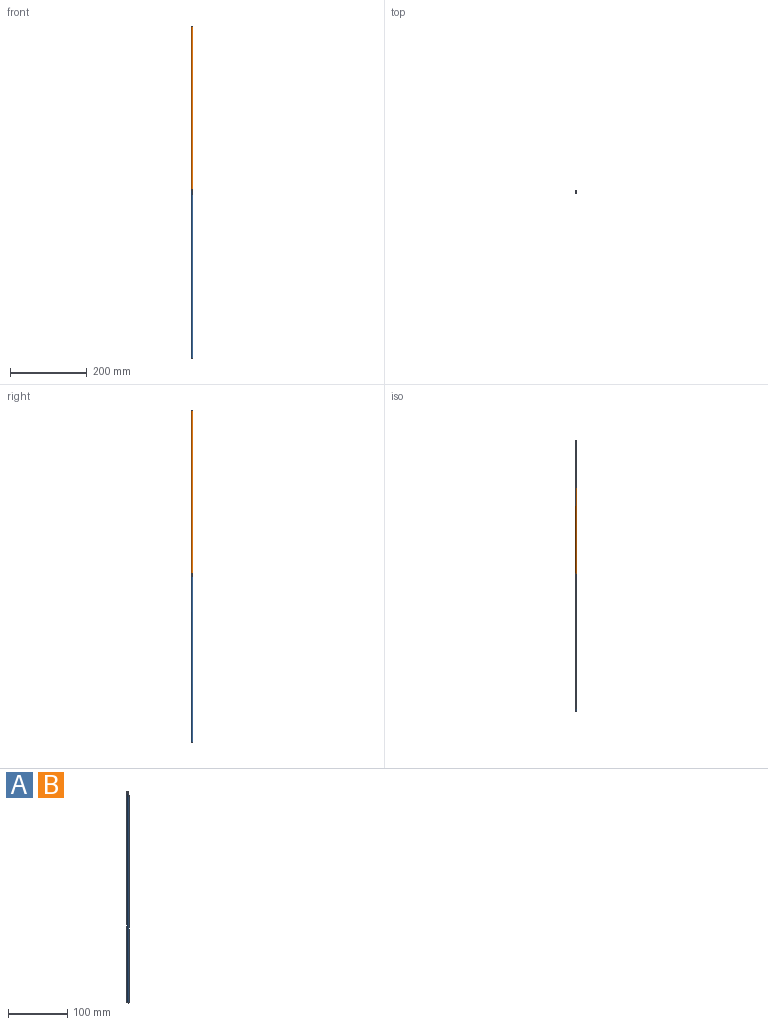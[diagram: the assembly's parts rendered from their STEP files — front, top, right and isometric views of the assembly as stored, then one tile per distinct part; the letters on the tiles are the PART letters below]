
ASSEMBLY  parts=2 mates=1
PART A: 6 faces, bbox 4x4x436 mm
  f0: plane 4x2mm, normal (0,0,1), area 6.3mm2, adj f1,f3
  f1: cylinder r=2mm len=436mm, axis (0,0,-1), area 5412.9mm2, adj f0,f2,f3,f4,f5
  f2: plane 4x4mm, normal (0,0,-1), area 12.6mm2, adj f1
  f3: plane 10x4mm, normal (1,0,0), area 36.9mm2, adj f0,f1,f4,f5
  f4: plane 4x2mm, normal (0,0,1), area 6.3mm2, adj f1,f3
  f5: cylinder r=1mm len=2mm, axis (1,0,0), area 11.7mm2, adj f1,f3
PART B: same geometry as A
PLACE A t=(-58.14,-8.62,-180.58)mm
PLACE B rot(axis=(0,1,0),180deg) t=(-58.14,-8.62,685.42)mm
MATE revolute B.f5 <-> A.f5  axis (-1,0,0) through (-58.14,-8.62,252.42)mm
